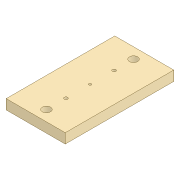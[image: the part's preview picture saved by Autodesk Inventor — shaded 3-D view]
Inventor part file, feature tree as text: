
AUTODESK INVENTOR PART (.ipt)
format: ipt  version: 2020 (Build 240168000, 168)  size: 113,152 bytes
history: native  units: mm
features: extrude x2, sketch x2, other x1, chamfer x1
ambient origin geometry x8: Origin, YZ Plane, XZ Plane, XY Plane, X Axis, Y Axis, Z Axis, Center Point
bodies: Body1 (feature_tree)
feature tree (6):
  other  "Sólido1"
  extrude  "Extrusão1"  Depth=12.0mm TaperAngle=0.0deg
  extrude  "Extrusão2"  Depth=53.1mm
  chamfer  "Chanfro1"  Distance=4.2mm
  sketch  "Esboço1"  dims[d0=69.9mm d1=12.0mm d2=0.0mm]
  sketch  "Esboço2"  dims[d3=3.0mm d4=4.2mm d5=4.2mm d6=12.0mm d7=0.0mm d8=2.5mm d9=2.0mm d10=45.0deg d11=132.363mm d12=72.0mm d13=10.0mm d14=53.1mm d15=10.0mm d16=53.1mm]
